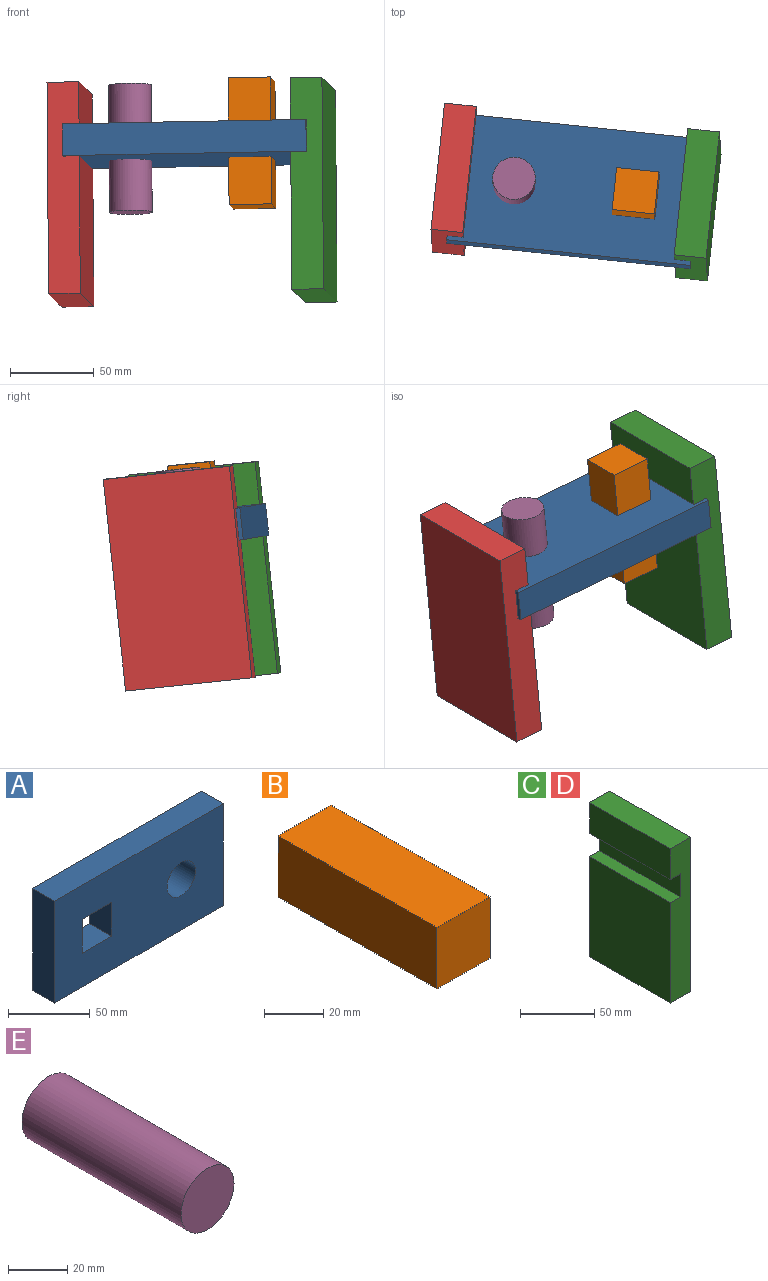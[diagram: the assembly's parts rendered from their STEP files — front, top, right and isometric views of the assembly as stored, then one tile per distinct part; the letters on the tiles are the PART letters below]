
ASSEMBLY  parts=5 mates=4
PART A: 11 faces, bbox 146.1x19.1x76.2 mm
  f0: plane 146.05x19.05mm, normal (0,0,-1), area 2782.3mm2, adj f1,f8,f9,f10
  f1: plane 76.2x19.05mm, normal (1,0,0), area 1451.6mm2, adj f0,f2,f9,f10
  f2: plane 146.05x19.05mm, normal (0,0,1), area 2782.3mm2, adj f1,f8,f9,f10
  f3: plane 25.4x19.05mm, normal (0,0,1), area 483.9mm2, adj f4,f6,f9,f10
  f4: plane 25.4x19.05mm, normal (1,0,0), area 483.9mm2, adj f3,f5,f9,f10
  f5: plane 25.4x19.05mm, normal (0,0,-1), area 483.9mm2, adj f4,f6,f9,f10
  f6: plane 25.4x19.05mm, normal (-1,0,0), area 483.9mm2, adj f3,f5,f9,f10
  f7: cylinder r=12.31mm len=24.61mm, axis (0,1,0), area 1472.9mm2, adj f9,f10
  f8: plane 76.2x19.05mm, normal (-1,0,0), area 1451.6mm2, adj f0,f2,f9,f10
  f9: plane 146.05x76.2mm, normal (0,-1,0), area 10008.1mm2, adj f0,f1,f2,f3,f4,f5,f6,f7
  f10: plane 146.05x76.2mm, normal (0,1,0), area 10008.1mm2, adj f0,f1,f2,f3,f4,f5,f6,f7
PART B: 6 faces, bbox 25.4x76.2x25.4 mm
  f0: plane 76.2x25.4mm, normal (1,0,0), area 1935.5mm2, adj f1,f3,f4,f5
  f1: plane 76.2x25.4mm, normal (0,0,1), area 1935.5mm2, adj f0,f2,f4,f5
  f2: plane 76.2x25.4mm, normal (-1,0,0), area 1935.5mm2, adj f1,f3,f4,f5
  f3: plane 76.2x25.4mm, normal (0,0,-1), area 1935.5mm2, adj f0,f2,f4,f5
  f4: plane 25.4x25.4mm, normal (0,-1,0), area 645.2mm2, adj f0,f1,f2,f3
  f5: plane 25.4x25.4mm, normal (0,1,0), area 645.2mm2, adj f0,f1,f2,f3
PART C: 10 faces, bbox 19.1x76.2x127 mm
  f0: plane 76.2x9.53mm, normal (0,0,1), area 725.8mm2, adj f1,f7,f8,f9
  f1: plane 82.55x76.2mm, normal (-1,0,0), area 6290.3mm2, adj f0,f2,f8,f9
  f2: plane 76.2x19.05mm, normal (0,0,-1), area 1451.6mm2, adj f1,f3,f8,f9
  f3: plane 127x76.2mm, normal (1,0,0), area 9677.4mm2, adj f2,f4,f8,f9
  f4: plane 76.2x19.05mm, normal (0,0,1), area 1451.6mm2, adj f3,f5,f8,f9
  f5: plane 76.2x25.4mm, normal (-1,0,0), area 1935.5mm2, adj f4,f6,f8,f9
  f6: plane 76.2x9.53mm, normal (0,0,-1), area 725.8mm2, adj f5,f7,f8,f9
  f7: plane 76.2x19.05mm, normal (-1,0,0), area 1451.6mm2, adj f0,f6,f8,f9
  f8: plane 127x19.05mm, normal (0,-1,0), area 2237.9mm2, adj f0,f1,f2,f3,f4,f5,f6,f7
  f9: plane 127x19.05mm, normal (0,1,0), area 2237.9mm2, adj f0,f1,f2,f3,f4,f5,f6,f7
PART D: same geometry as C
PART E: 3 faces, bbox 25.4x76.2x25.4 mm
  f0: cylinder r=12.7mm len=76.2mm, axis (0,1,0), area 6080.5mm2, adj f1,f2
  f1: plane 25.4x25.4mm, normal (0,-1,0), area 506.7mm2, adj f0
  f2: plane 25.4x25.4mm, normal (0,1,0), area 506.7mm2, adj f0
PLACE A rot(axis=(0.03,0.74,0.67),175.2deg) t=(-95.52,-20.23,121.51)mm
PLACE B rot(axis=(-0.64,-0.52,0.57),120.6deg) t=(-12.53,35.49,68.34)mm
PLACE C rot(axis=(-0.7,-0.09,-0.71),8.6deg) t=(-4.65,31.97,87.86)mm
PLACE D rot(axis=(-0.01,0.05,1),174deg) t=(-182.3,-25.55,92.64)mm
PLACE E rot(axis=(1,-0.06,-0.05),84.2deg) t=(-162.32,55.06,139.63)mm
MATE planar B.f0 <-> A.f5  axis (0.11,0.99,-0.1) through (-56.24,11.41,108.88)mm
MATE cylindrical E.f0 <-> A.f7  axis (-0.01,0.11,0.99) through (-129.89,2.25,68.83)mm
MATE planar C.f7 <-> A.f8  axis (-0.99,0.1,-0.02) through (-21,-2.41,110.6)mm
MATE planar D.f7 <-> A.f1  axis (0.99,-0.1,0.02) through (-166.23,12.86,107.91)mm
